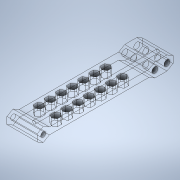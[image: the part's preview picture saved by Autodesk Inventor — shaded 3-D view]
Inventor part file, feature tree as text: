
AUTODESK INVENTOR PART (.ipt)
format: ipt  version: 2020 (Build 240168000, 168)  size: 371,712 bytes
history: native  units: in
note: dims shown in document units (in); Inventor stores cm internally (conversion verified against a paired STEP export)
features: sketch x6, extrude x5, projected_geometry x3, plane x1, mirror x1
ambient origin geometry x8: Origin, YZ Plane, XZ Plane, XY Plane, X Axis, Y Axis, Z Axis, Center Point
bodies: Solid1 (feature_tree)
feature tree (16):
  extrude  "Extrusion1"  Depth=3.5433in
  plane  "Work Plane1"
  extrude  "Extrusion2"  Depth=0.7874in
  extrude  "Extrusion3"  Depth=0.0787in
  sketch  "Sketch4"  dims[d6=0.7874in d7=0.0in d8=0.0787in]
  extrude  "Extrusion4"  Depth=0.0787in
  extrude  "Extrusion5"  Depth=0.0787in
  mirror  "Mirror1"
  sketch  "Sketch1"  dims[d0=0.1818in d1=3.5433in]
  sketch  "Sketch2"  dims[d2=0.1299in d3=0.7874in]
  sketch  "Sketch3"  dims[d4=0.0in d5=0.0787in]
  projected_geometry  "Projected Loop1"
  sketch  "Sketch5"  dims[d9=0.0787in d10=0.0787in]
  sketch  "Sketch6"  dims[d11=0.2273in d12=3.937in d14=0.2903in d15=0.3937in d17=0.3937in d19=3.937in d21=0.2903in d22=0.3937in d24=0.3937in d26=0.7874in d27=0.0in d28=3.2283in d29=0.315in d30=0.315in d31=0.315in d33=0.1575in d34=0.2362in d35=0.0in d36=0.2756in d37=-0.3092in]
  projected_geometry  "Projected Loop2"
  projected_geometry  "Projected Loop3"
